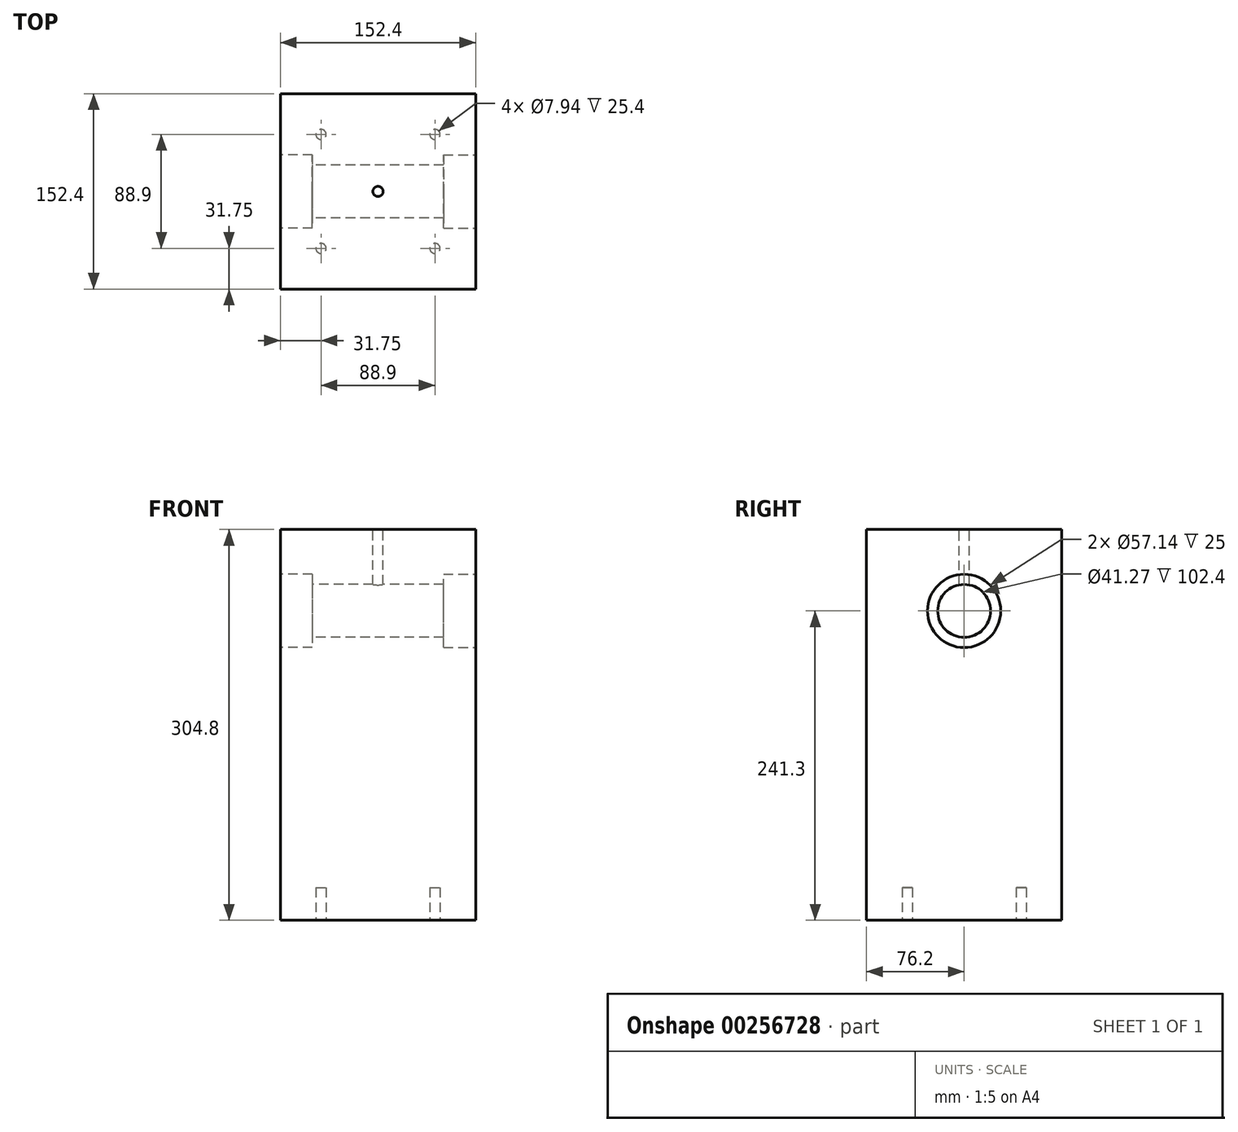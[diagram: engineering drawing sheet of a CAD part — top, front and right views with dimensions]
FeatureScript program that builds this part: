
annotation { "Feature Type Name" : "Feature", "Feature Type Description" : "" }
export const myFeature = defineFeature(function(context is Context, id is Id, definition is map)
    precondition{}
    {
        {
            var Q0;
            Q0=qCreatedBy(makeId("Top.planeOp"),FACE);
            var sketch = newSketch(context, id + "F0", { "sketchPlane" : qUnion([Q0])});
            skLineSegment(sketch, "E0.bottom", {"start": v(0, 0) * mm, "end": v(152.4, 0) * mm});
            skLineSegment(sketch, "E0.top", {"start": v(0, 152.4) * mm, "end": v(152.4, 152.4) * mm});
            skLineSegment(sketch, "E0.left", {"start": v(0, 0) * mm, "end": v(0, 152.4) * mm});
            skLineSegment(sketch, "E0.right", {"start": v(152.4, 0) * mm, "end": v(152.4, 152.4) * mm});
            skSolve(sketch);
        }
        {
            var Q0;
            Q0=makeQuery(id+"F0.imprint","IMPRINT",FACE,{"disambiguationData":[TD([[makeQuery(id+"F0.imprint","IMPRINT",EDGE,{"derivedFrom":sQuery(id+"F0.wireOp",EDGE,"E0.bottom")}),1.0]])]});
            extrude(context, id + "F1", {"entities" : qUnion([Q0]), "depth" : 304.8 * mm});
        }
        {
            var Q0;
            Q0=makeQuery(id+"F1.opExtrude","SWEPT_FACE",FACE,{"disambiguationData":[OSD([sQuery(id+"F0.wireOp",EDGE,"E0.right")])]});
            var sketch = newSketch(context, id + "F2", { "sketchPlane" : qUnion([Q0])});
            skLineSegment(sketch, "E1", {"start": v(76.2, 304.8) * mm, "end": v(76.2, 177.8) * mm, "construction": true});
            skCircle(sketch, "E2", {"center": v(76.2, 241.3) * mm, "radius": 28.57 * mm});
            skSolve(sketch);
        }
        {
            var Q0;
            Q0=makeQuery(id+"F2.imprint","IMPRINT",FACE,{"disambiguationData":[TD([[makeQuery(id+"F2.imprint","IMPRINT",EDGE,{"derivedFrom":sQuery(id+"F2.wireOp",EDGE,"E2")}),1.0]])]});
            extrude(context, id + "F3", {"entities" : qUnion([Q0]), "operationType" : NewBodyOperationType.REMOVE, "oppositeDirection" : true, "depth" : 25 * mm});
        }
        {
            var Q0;
            Q0=makeQuery(id+"F1.opExtrude","SWEPT_FACE",FACE,{"disambiguationData":[OSD([sQuery(id+"F0.wireOp",EDGE,"E0.left")])]});
            var sketch = newSketch(context, id + "F4", { "sketchPlane" : qUnion([Q0])});
            skLineSegment(sketch, "E3", {"start": v(-76.2, 304.8) * mm, "end": v(-76.2, 177.8) * mm, "construction": true});
            skCircle(sketch, "E4", {"center": v(-76.2, 241.3) * mm, "radius": 28.57 * mm});
            skSolve(sketch);
        }
        {
            var Q0;
            Q0=makeQuery(id+"F4.imprint","IMPRINT",FACE,{"disambiguationData":[TD([[makeQuery(id+"F4.imprint","IMPRINT",EDGE,{"derivedFrom":sQuery(id+"F4.wireOp",EDGE,"E4")}),1.0]])]});
            extrude(context, id + "F5", {"entities" : qUnion([Q0]), "operationType" : NewBodyOperationType.REMOVE, "oppositeDirection" : true, "depth" : 25 * mm});
        }
        {
            var Q0;
            Q0=makeQuery(id+"F5.boolean.opBoolean","COPY",FACE,{"derivedFrom":makeQuery(id+"F5.opExtrude","CAP_FACE",FACE,{"disambiguationData":[OSD([sQuery(id+"F4.wireOp",EDGE,"E4")])],"isStart":false})});
            var sketch = newSketch(context, id + "F6", { "sketchPlane" : qUnion([Q0])});
            skCircle(sketch, "E5", {"center": v(-76.2, 241.3) * mm, "radius": 20.64 * mm});
            skSolve(sketch);
        }
        {
            var Q0;
            Q0 = qSketchRegion(id + "F6", true);
            extrude(context, id + "F7", {"entities" : qUnion([Q0]), "operationType" : NewBodyOperationType.REMOVE, "oppositeDirection" : true, "depth" : 264.16 * mm});
        }
        {
            var Q0;
            Q0=makeQuery(id+"F1.opExtrude","CAP_FACE",FACE,{"disambiguationData":[OSD([sQuery(id+"F0.wireOp",EDGE,"E0.bottom"),sQuery(id+"F0.wireOp",EDGE,"E0.top"),sQuery(id+"F0.wireOp",EDGE,"E0.left"),sQuery(id+"F0.wireOp",EDGE,"E0.right")])],"isStart":true});
            var sketch = newSketch(context, id + "F8", { "sketchPlane" : qUnion([Q0])});
            skLineSegment(sketch, "E6", {"start": v(0, -76.2) * mm, "end": v(152.4, -76.2) * mm, "construction": true});
            skLineSegment(sketch, "E7", {"start": v(76.2, 0) * mm, "end": v(76.2, -152.4) * mm, "construction": true});
            skLineSegment(sketch, "E8.bottom", {"start": v(120.65, -31.75) * mm, "end": v(31.75, -31.75) * mm, "construction": true});
            skLineSegment(sketch, "E8.top", {"start": v(120.65, -120.65) * mm, "end": v(31.75, -120.65) * mm, "construction": true});
            skLineSegment(sketch, "E8.left", {"start": v(120.65, -31.75) * mm, "end": v(120.65, -120.65) * mm, "construction": true});
            skLineSegment(sketch, "E8.right", {"start": v(31.75, -31.75) * mm, "end": v(31.75, -120.65) * mm, "construction": true});
            skPoint(sketch, "E8.middle", {"position": v(76.2, -76.2) * mm});
            skCircle(sketch, "E9", {"center": v(31.75, -31.75) * mm, "radius": 3.97 * mm});
            skCircle(sketch, "E10", {"center": v(120.65, -31.75) * mm, "radius": 3.97 * mm});
            skCircle(sketch, "E11", {"center": v(31.75, -120.65) * mm, "radius": 3.97 * mm});
            skCircle(sketch, "E12", {"center": v(120.65, -120.65) * mm, "radius": 3.97 * mm});
            skSolve(sketch);
        }
        {
            var Q0;
            Q0=makeQuery(id+"F8.imprint","IMPRINT",FACE,{"disambiguationData":[TD([[makeQuery(id+"F8.imprint","IMPRINT",EDGE,{"derivedFrom":sQuery(id+"F8.wireOp",EDGE,"E9")}),1.0]])]});
            var Q1;
            Q1=makeQuery(id+"F8.imprint","IMPRINT",FACE,{"disambiguationData":[TD([[makeQuery(id+"F8.imprint","IMPRINT",EDGE,{"derivedFrom":sQuery(id+"F8.wireOp",EDGE,"E10")}),1.0]])]});
            var Q2;
            Q2=makeQuery(id+"F8.imprint","IMPRINT",FACE,{"disambiguationData":[TD([[makeQuery(id+"F8.imprint","IMPRINT",EDGE,{"derivedFrom":sQuery(id+"F8.wireOp",EDGE,"E12")}),1.0]])]});
            var Q3;
            Q3=makeQuery(id+"F8.imprint","IMPRINT",FACE,{"disambiguationData":[TD([[makeQuery(id+"F8.imprint","IMPRINT",EDGE,{"derivedFrom":sQuery(id+"F8.wireOp",EDGE,"E11")}),1.0]])]});
            extrude(context, id + "F9", {"entities" : qUnion([Q0, Q1, Q2, Q3]), "operationType" : NewBodyOperationType.REMOVE, "oppositeDirection" : true, "depth" : 25.4 * mm});
        }
        {
            var Q0;
            Q0=makeQuery(id+"F1.opExtrude","CAP_FACE",FACE,{"disambiguationData":[OSD([sQuery(id+"F0.wireOp",EDGE,"E0.bottom"),sQuery(id+"F0.wireOp",EDGE,"E0.top"),sQuery(id+"F0.wireOp",EDGE,"E0.left"),sQuery(id+"F0.wireOp",EDGE,"E0.right")])],"isStart":false});
            var sketch = newSketch(context, id + "F10", { "sketchPlane" : qUnion([Q0])});
            skLineSegment(sketch, "E13", {"start": v(0, 152.4) * mm, "end": v(152.4, 0) * mm, "construction": true});
            skLineSegment(sketch, "E14", {"start": v(0, 0) * mm, "end": v(152.4, 152.4) * mm, "construction": true});
            skCircle(sketch, "E15", {"center": v(76.2, 76.2) * mm, "radius": 3.97 * mm});
            skSolve(sketch);
        }
        {
            var Q0;
            Q0 = qSketchRegion(id + "F10", true);
            extrude(context, id + "F11", {"entities" : qUnion([Q0]), "operationType" : NewBodyOperationType.REMOVE, "oppositeDirection" : true, "depth" : 48.26 * mm});
        }
    });
